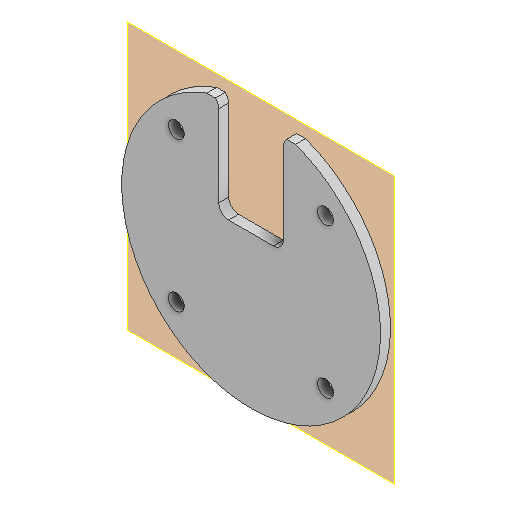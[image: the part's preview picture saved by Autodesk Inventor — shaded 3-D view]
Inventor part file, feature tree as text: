
AUTODESK INVENTOR PART (.ipt)
format: ipt  version: 2022 (Build 260153000, 153)  size: 149,504 bytes
history: native  units: mm
features: reference x6, plane x2, extrude x2, sketch x2, other x2, hole x1, fillet x1, projected_geometry x1
ambient origin geometry x8: Origin, YZ Plane, XZ Plane, XY Plane, X Axis, Y Axis, Z Axis, Center Point
bodies: Volumenkörper1 (feature_tree)
feature tree (17):
  plane  "Arbeitsebene1"
  extrude  "Extrusion1"  Depth=4.0mm
  plane  "Arbeitsebene2"
  hole  "Bohrung1"  [1 undecoded]
  extrude  "Extrusion2"  Depth=2.0mm
  fillet  "Rundung1"  [1 undecoded]
  sketch  "Skizze1"  dims[d0=4.0mm d1=4.0mm]
  reference  "Referenz1"
  sketch  "Skizze2"  dims[d2=2.0mm d3=0.0mm d4=3.2mm d5=6.0mm d6=4.0mm d7=2.0mm d8=90.0deg d9=8.0mm d10=20.594885mm d11=10.0mm d12=0.0mm d13=2.0mm]
  projected_geometry  "Projizierte Kontur1"
  reference  "Referenz2"
  reference  "Referenz3"
  reference  "Referenz4"
  reference  "Referenz5"
  reference  "Referenz6"
  other  "Assembly_Cube_SEEED_Xiao_Sense_Camera_v3.iam"
  other  "20_Cube_Insert_SEEED_Xiao_Sense_Camera:1"
note: 2 required parameter values undecoded (feature->parameter linkage not recoverable at this tier; creation-order binding heuristic only, values carry confidence <= 0.55)
